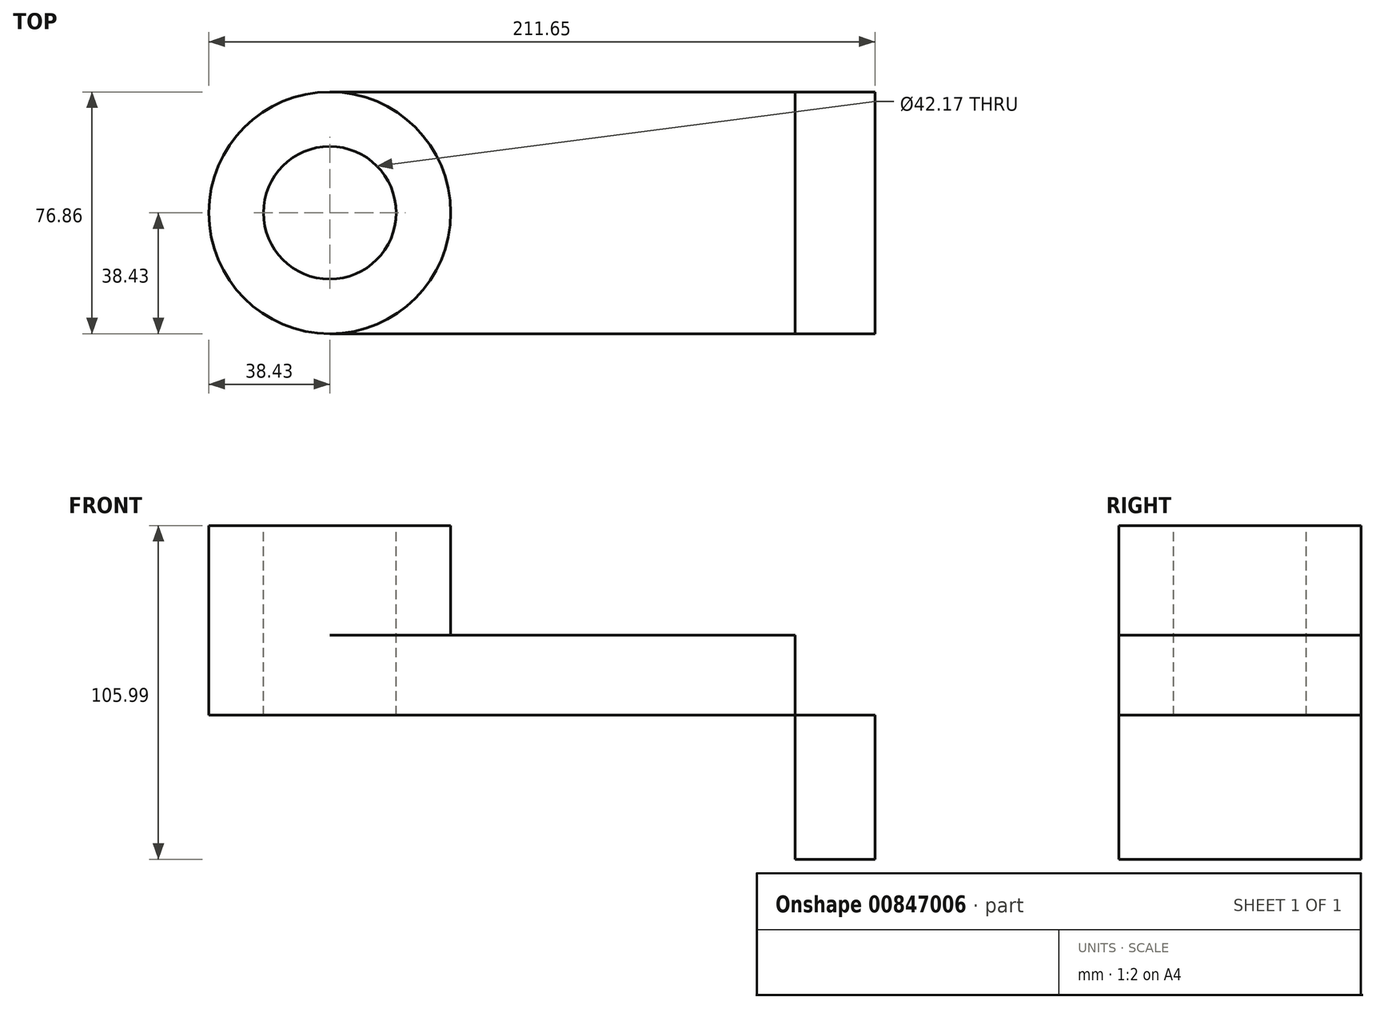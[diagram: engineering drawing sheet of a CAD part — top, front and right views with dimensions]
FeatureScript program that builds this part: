
annotation { "Feature Type Name" : "Feature", "Feature Type Description" : "" }
export const myFeature = defineFeature(function(context is Context, id is Id, definition is map)
    precondition{}
    {
        {
            var Q0;
            Q0=qCreatedBy(makeId("Top.planeOp"),FACE);
            var sketch = newSketch(context, id + "F0", { "sketchPlane" : qUnion([Q0])});
            skLineSegment(sketch, "E0.bottom", {"start": v(73.91, -38.43) * mm, "end": v(-73.91, -38.43) * mm});
            skLineSegment(sketch, "E0.top", {"start": v(73.91, 38.43) * mm, "end": v(-73.91, 38.43) * mm});
            skLineSegment(sketch, "E0.left", {"start": v(73.91, -38.43) * mm, "end": v(73.91, 38.43) * mm});
            skLineSegment(sketch, "E0.right", {"start": v(-73.91, -38.43) * mm, "end": v(-73.91, 38.43) * mm});
            skPoint(sketch, "E0.middle", {"position": v(0, 0) * mm});
            skCircle(sketch, "E1", {"center": v(-73.91, 0) * mm, "radius": 38.43 * mm});
            skSolve(sketch);
        }
        {
            var Q0;
            {var subQ0=sQuery(id+"F0.wireOp",EDGE,"E0.right");Q0=makeQuery(id+"F0.imprint","IMPRINT",FACE,{"disambiguationData":[TD([[makeQuery(id+"F0.imprint","IMPRINT",EDGE,{"derivedFrom":subQ0}),1.0]])]});}
            var Q1;
            {var subQ0=sQuery(id+"F0.wireOp",EDGE,"E0.bottom");Q1=makeQuery(id+"F0.imprint","IMPRINT",FACE,{"disambiguationData":[TD([[makeQuery(id+"F0.imprint","IMPRINT",EDGE,{"derivedFrom":subQ0}),-1.0]])]});}
            var Q2;
            {var subQ0=sQuery(id+"F0.wireOp",EDGE,"E0.right");Q2=makeQuery(id+"F0.imprint","IMPRINT",FACE,{"disambiguationData":[TD([[makeQuery(id+"F0.imprint","IMPRINT",EDGE,{"derivedFrom":subQ0}),-1.0]])]});}
            extrude(context, id + "F1", {"entities" : qUnion([Q0, Q1, Q2]), "depth" : 25.4 * mm, "offsetDistance" : 25.4 * mm});
        }
        {
            var Q0;
            {var subQ0=sQuery(id+"F0.wireOp",EDGE,"E0.right");Q0=makeQuery(id+"F0.imprint","IMPRINT",FACE,{"disambiguationData":[TD([[makeQuery(id+"F0.imprint","IMPRINT",EDGE,{"derivedFrom":subQ0}),1.0]])]});}
            var Q1;
            {var subQ0=sQuery(id+"F0.wireOp",EDGE,"E0.right");Q1=makeQuery(id+"F0.imprint","IMPRINT",FACE,{"disambiguationData":[TD([[makeQuery(id+"F0.imprint","IMPRINT",EDGE,{"derivedFrom":subQ0}),-1.0]])]});}
            extrude(context, id + "F2", {"entities" : qUnion([Q0, Q1]), "operationType" : NewBodyOperationType.ADD, "depth" : 60.2 * mm, "offsetDistance" : 25.4 * mm});
        }
        {
            var Q0;
            {var subQ0=sQuery(id+"F0.wireOp",EDGE,"E0.bottom");Q0=makeQuery(id+"F0.imprint","IMPRINT",FACE,{"disambiguationData":[TD([[makeQuery(id+"F0.imprint","IMPRINT",EDGE,{"derivedFrom":subQ0}),-1.0]])]});}
            var sketch = newSketch(context, id + "F3", { "sketchPlane" : qUnion([Q0])});
            skCircle(sketch, "E2", {"center": v(-73.3, 0) * mm, "radius": 19.7 * mm});
            skSolve(sketch);
        }
        {
            var Q0;
            Q0=makeQuery(id+"F3.imprint","IMPRINT",FACE,{"disambiguationData":[TD([[makeQuery(id+"F3.imprint","IMPRINT",EDGE,{"derivedFrom":sQuery(id+"F3.wireOp",EDGE,"E2")}),1.0]])]});
            extrude(context, id + "F4", {"entities" : qUnion([Q0]), "operationType" : NewBodyOperationType.REMOVE, "oppositeDirection" : true, "depth" : 25.4 * mm, "offsetDistance" : 25.4 * mm});
        }
        {
            var Q0;
            Q0=makeQuery(id+"F2.opExtrude","CAP_FACE",FACE,{"disambiguationData":[OSD([sQuery(id+"F0.wireOp",EDGE,"E1")])],"isStart":false});
            var sketch = newSketch(context, id + "F5", { "sketchPlane" : qUnion([Q0])});
            skCircle(sketch, "E3", {"center": v(-73.91, 0) * mm, "radius": 21.09 * mm});
            skSolve(sketch);
        }
        {
            var Q0;
            Q0=makeQuery(id+"F5.imprint","IMPRINT",FACE,{"disambiguationData":[TD([[makeQuery(id+"F5.imprint","IMPRINT",EDGE,{"derivedFrom":sQuery(id+"F5.wireOp",EDGE,"E3")}),1.0]])]});
            extrude(context, id + "F6", {"entities" : qUnion([Q0]), "operationType" : NewBodyOperationType.REMOVE, "oppositeDirection" : true, "depth" : 62.16 * mm, "offsetDistance" : 25.4 * mm});
        }
        {
            var Q0;
            Q0=makeQuery(id+"F1.opExtrude","SWEPT_FACE",FACE,{"disambiguationData":[OSD([sQuery(id+"F0.wireOp",EDGE,"E0.left")])]});
            var sketch = newSketch(context, id + "F7", { "sketchPlane" : qUnion([Q0])});
            skLineSegment(sketch, "E4.bottom", {"start": v(38.43, 0) * mm, "end": v(-38.43, 0) * mm});
            skLineSegment(sketch, "E4.top", {"start": v(38.43, -45.78) * mm, "end": v(-38.43, -45.78) * mm});
            skLineSegment(sketch, "E4.left", {"start": v(38.43, 0) * mm, "end": v(38.43, -45.78) * mm});
            skLineSegment(sketch, "E4.right", {"start": v(-38.43, 0) * mm, "end": v(-38.43, -45.78) * mm});
            skSolve(sketch);
        }
        {
            var Q0;
            Q0=makeQuery(id+"F7.imprint","IMPRINT",FACE,{"disambiguationData":[TD([[makeQuery(id+"F7.imprint","IMPRINT",EDGE,{"derivedFrom":sQuery(id+"F7.wireOp",EDGE,"E4.bottom")}),-1.0]])]});
            extrude(context, id + "F8", {"entities" : qUnion([Q0]), "depth" : 25.4 * mm, "offsetDistance" : 25.4 * mm});
        }
    });
